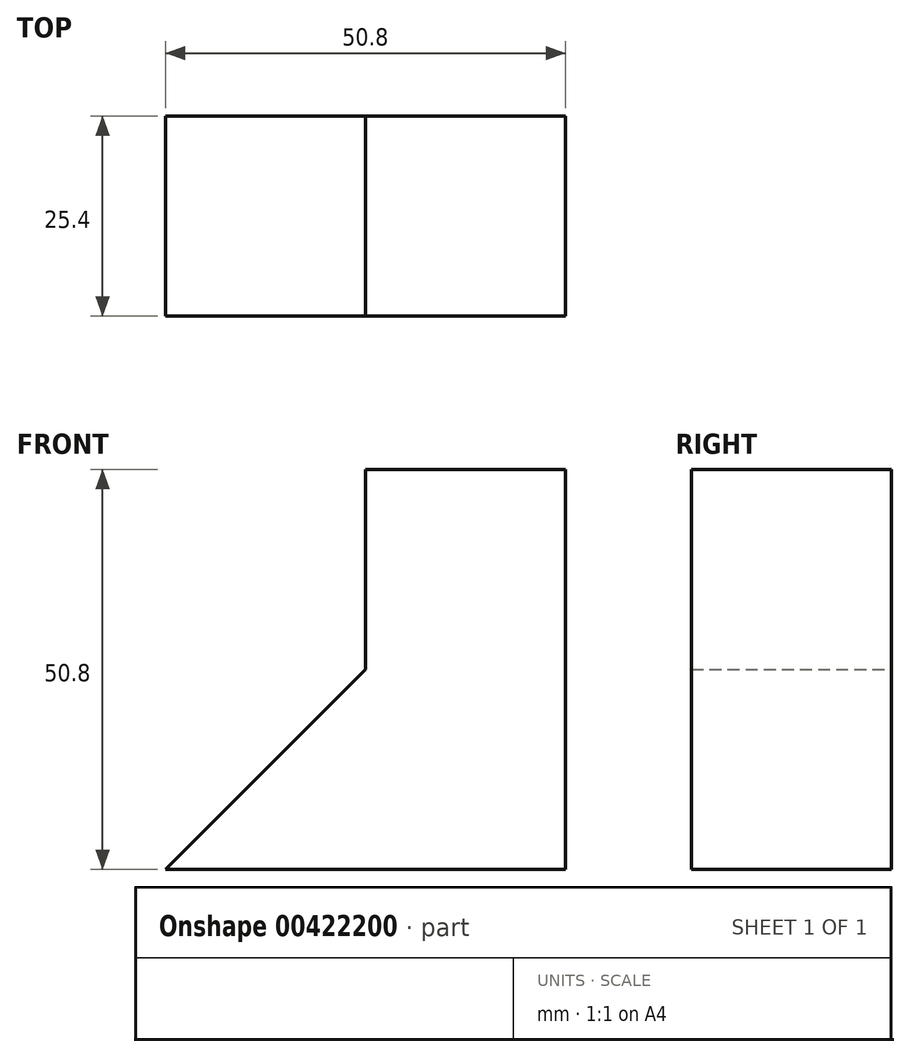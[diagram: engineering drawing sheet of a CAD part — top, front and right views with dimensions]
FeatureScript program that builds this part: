
annotation { "Feature Type Name" : "Feature", "Feature Type Description" : "" }
export const myFeature = defineFeature(function(context is Context, id is Id, definition is map)
    precondition{}
    {
        {
            var Q0;
            Q0=qCreatedBy(makeId("Front.planeOp"),FACE);
            var sketch = newSketch(context, id + "F0", { "sketchPlane" : qUnion([Q0])});
            skLineSegment(sketch, "E0", {"start": v(0, 0) * mm, "end": v(-50.8, 0) * mm});
            skLineSegment(sketch, "E1", {"start": v(0, 0) * mm, "end": v(0, 50.8) * mm});
            skLineSegment(sketch, "E2", {"start": v(0, 50.8) * mm, "end": v(-25.4, 50.8) * mm});
            skLineSegment(sketch, "E3", {"start": v(-25.4, 50.8) * mm, "end": v(-25.4, 25.4) * mm});
            skLineSegment(sketch, "E4", {"start": v(-25.4, 25.4) * mm, "end": v(-50.8, 0) * mm});
            skSolve(sketch);
        }
        {
            var Q0;
            Q0=makeQuery(id+"F0.imprint","IMPRINT",FACE,{"disambiguationData":[TD([[makeQuery(id+"F0.imprint","IMPRINT",EDGE,{"derivedFrom":sQuery(id+"F0.wireOp",EDGE,"E0")}),-1.0]])]});
            extrude(context, id + "F1", {"entities" : qUnion([Q0]), "depth" : 25.4 * mm});
        }
    });
